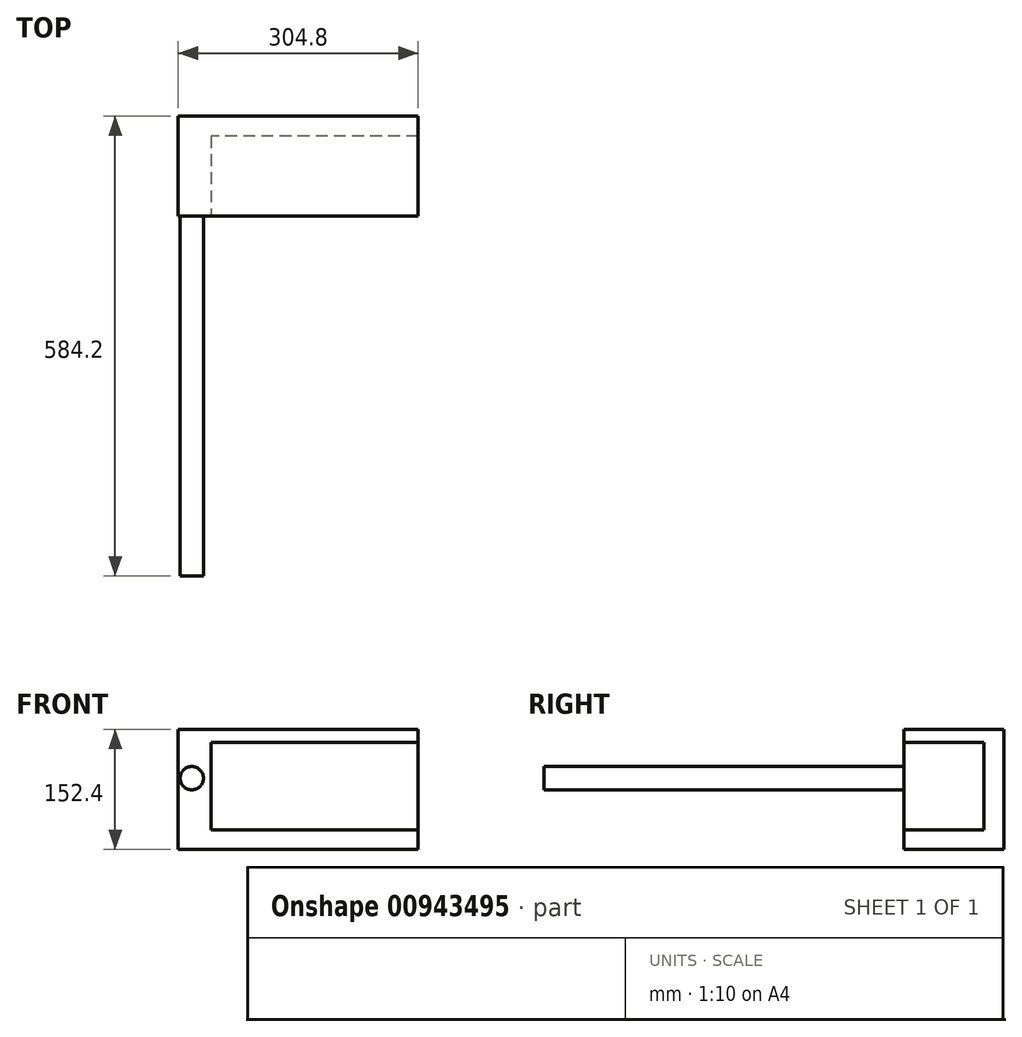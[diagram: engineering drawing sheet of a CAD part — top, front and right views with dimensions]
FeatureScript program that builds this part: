
annotation { "Feature Type Name" : "Feature", "Feature Type Description" : "" }
export const myFeature = defineFeature(function(context is Context, id is Id, definition is map)
    precondition{}
    {
        {
            var Q0;
            Q0=qCreatedBy(makeId("Front.planeOp"),FACE);
            var sketch = newSketch(context, id + "F0", { "sketchPlane" : qUnion([Q0])});
            skLineSegment(sketch, "E0.bottom", {"start": v(152.4, -76.2) * mm, "end": v(-152.4, -76.2) * mm});
            skLineSegment(sketch, "E0.top", {"start": v(152.4, 76.2) * mm, "end": v(-152.4, 76.2) * mm});
            skLineSegment(sketch, "E0.left", {"start": v(152.4, -76.2) * mm, "end": v(152.4, 76.2) * mm});
            skLineSegment(sketch, "E0.right", {"start": v(-152.4, -76.2) * mm, "end": v(-152.4, 76.2) * mm});
            skPoint(sketch, "E0.middle", {"position": v(0, 0) * mm});
            skSolve(sketch);
        }
        {
            var Q0;
            Q0 = qSketchRegion(id + "F0", true);
            extrude(context, id + "F1", {"entities" : qUnion([Q0]), "depth" : 127 * mm, "offsetDistance" : 25.4 * mm});
        }
        {
            var Q0;
            Q0=makeQuery(id+"F1.opExtrude","CAP_FACE",FACE,{"disambiguationData":[OSD([sQuery(id+"F0.wireOp",EDGE,"E0.bottom"),sQuery(id+"F0.wireOp",EDGE,"E0.top"),sQuery(id+"F0.wireOp",EDGE,"E0.left"),sQuery(id+"F0.wireOp",EDGE,"E0.right")])],"isStart":false});
            var sketch = newSketch(context, id + "F2", { "sketchPlane" : qUnion([Q0])});
            skLineSegment(sketch, "E1.bottom", {"start": v(152.4, 60.03) * mm, "end": v(-110.36, 60.03) * mm});
            skLineSegment(sketch, "E1.top", {"start": v(152.4, -51.7) * mm, "end": v(-110.36, -51.7) * mm});
            skLineSegment(sketch, "E1.left", {"start": v(152.4, 60.03) * mm, "end": v(152.4, -51.7) * mm});
            skLineSegment(sketch, "E1.right", {"start": v(-110.36, 60.03) * mm, "end": v(-110.36, -51.7) * mm});
            skSolve(sketch);
        }
        {
            var Q0;
            Q0 = qSketchRegion(id + "F2", true);
            extrude(context, id + "F3", {"entities" : qUnion([Q0]), "operationType" : NewBodyOperationType.REMOVE, "endBound" : BoundingType.SYMMETRIC, "oppositeDirection" : true, "depth" : 203.2 * mm, "offsetDistance" : 25.4 * mm});
        }
        {
            var Q0;
            Q0=makeQuery(id+"F1.opExtrude","CAP_FACE",FACE,{"disambiguationData":[OSD([sQuery(id+"F0.wireOp",EDGE,"E0.bottom"),sQuery(id+"F0.wireOp",EDGE,"E0.top"),sQuery(id+"F0.wireOp",EDGE,"E0.left"),sQuery(id+"F0.wireOp",EDGE,"E0.right")])],"isStart":false});
            var sketch = newSketch(context, id + "F4", { "sketchPlane" : qUnion([Q0])});
            skCircle(sketch, "E2", {"center": v(-135.15, 14.28) * mm, "radius": 14.82 * mm});
            skSolve(sketch);
        }
        {
            var Q0;
            Q0=makeQuery(id+"F4.imprint","IMPRINT",FACE,{"disambiguationData":[TD([[makeQuery(id+"F4.imprint","IMPRINT",EDGE,{"derivedFrom":sQuery(id+"F4.wireOp",EDGE,"E2")}),1.0]])]});
            extrude(context, id + "F5", {"entities" : qUnion([Q0]), "operationType" : NewBodyOperationType.ADD, "depth" : 457.2 * mm, "offsetDistance" : 25.4 * mm});
        }
    });
